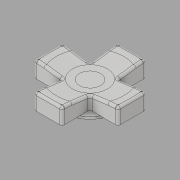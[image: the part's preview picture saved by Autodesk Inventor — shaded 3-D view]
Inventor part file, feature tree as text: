
AUTODESK INVENTOR PART (.ipt)
format: ipt  version: 2019 (Build 230136000, 136)  size: 416,256 bytes
history: native  units: mm
features: fillet x6, extrude x5, sketch x4, chamfer x2
ambient origin geometry x8: Origin, YZ Plane, XZ Plane, XY Plane, X Axis, Y Axis, Z Axis, Center Point
bodies: Solid1 (feature_tree)
feature tree (17):
  sketch  "Sketch1"  dims[d0=18.0mm d1=6.0mm]
  extrude  "Extrusion1"  Depth=6.0mm
  extrude  "Extrusion2"  Depth=18.0mm
  extrude  "Extrusion4"  Depth=0.5mm TaperAngle=0.0deg
  chamfer  "Chamfer5"  Distance=3.4mm
  fillet  "Fillet6"  Radius=0.5mm
  fillet  "Fillet7"  Radius=6.0mm
  fillet  "Fillet8"  Radius=0.75mm
  extrude  "Extrusion5"  Depth=0.5mm
  extrude  "Extrusion6"  Depth=10.0mm
  chamfer  "Chamfer6"  Distance=0.01mm
  fillet  "Fillet11"  Radius=3.0mm
  fillet  "Fillet12"  Radius=15.0mm
  fillet  "Fillet14"  Radius=15.0mm
  sketch  "Sketch3"  dims[d2=6.0mm d3=18.0mm]
  sketch  "Sketch4"  dims[d4=12.0mm d5=0.5mm d6=0.0mm d7=3.4mm d8=0.0mm d30=0.5mm d31=6.0mm d32=0.75mm d33=0.0mm]
  sketch  "Sketch5"  dims[d34=5.0mm d35=0.75mm d36=45.0deg d37=0.5mm d38=10.0mm d39=0.01mm d42=3.0mm d43=15.0mm d44=15.0mm d45=3.0mm d46=0.5mm d47=0.5mm d48=2.0mm d49=0.0mm d50=2.5mm d51=3.5mm d52=0.0mm d53=3.0mm d54=0.5mm d55=0.2mm d56=45.0deg d57=2.0mm d58=0.1mm d59=1.5mm d61=0.2mm]
